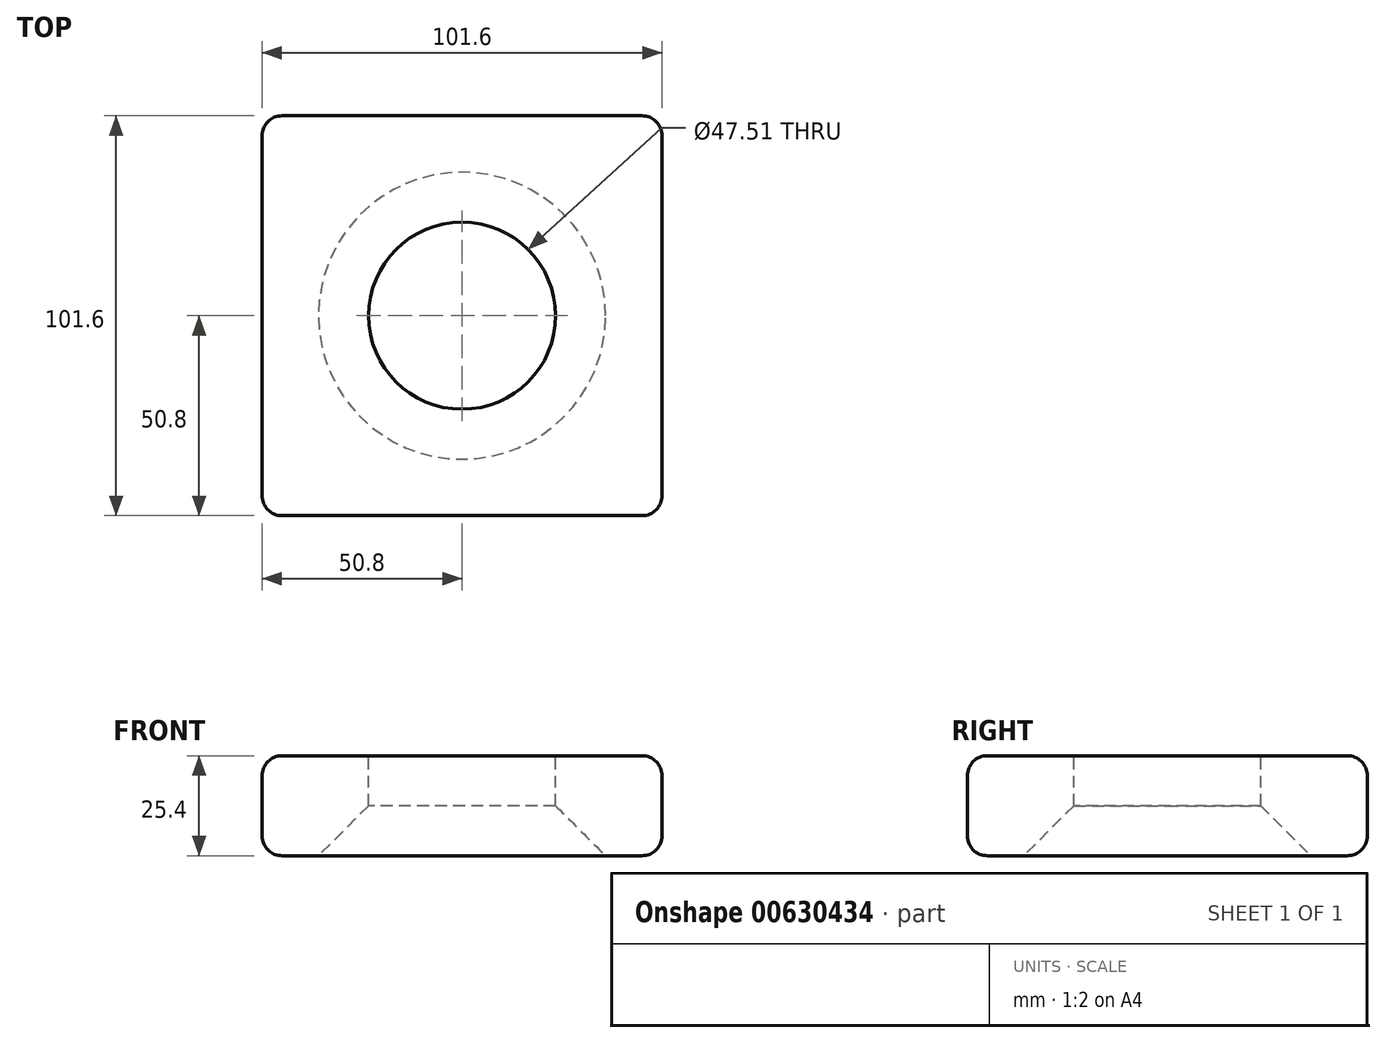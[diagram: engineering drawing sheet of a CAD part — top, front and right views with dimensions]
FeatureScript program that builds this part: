
annotation { "Feature Type Name" : "Feature", "Feature Type Description" : "" }
export const myFeature = defineFeature(function(context is Context, id is Id, definition is map)
    precondition{}
    {
        {
            var Q0;
            Q0=qCreatedBy(makeId("Top.planeOp"),FACE);
            var sketch = newSketch(context, id + "F0", { "sketchPlane" : qUnion([Q0])});
            skLineSegment(sketch, "E0.bottom", {"start": v(-50.8, 50.8) * mm, "end": v(50.8, 50.8) * mm});
            skLineSegment(sketch, "E0.top", {"start": v(-50.8, -50.8) * mm, "end": v(50.8, -50.8) * mm});
            skLineSegment(sketch, "E0.left", {"start": v(-50.8, 50.8) * mm, "end": v(-50.8, -50.8) * mm});
            skLineSegment(sketch, "E0.right", {"start": v(50.8, 50.8) * mm, "end": v(50.8, -50.8) * mm});
            skSolve(sketch);
        }
        {
            var Q0;
            Q0=makeQuery(id+"F0.imprint","IMPRINT",FACE,{"disambiguationData":[TD([[makeQuery(id+"F0.imprint","IMPRINT",EDGE,{"derivedFrom":sQuery(id+"F0.wireOp",EDGE,"E0.bottom")}),-1.0]])]});
            extrude(context, id + "F1", {"entities" : qUnion([Q0]), "oppositeDirection" : true, "depth" : 25.4 * mm, "offsetDistance" : 25.4 * mm});
        }
        {
            var Q0;
            Q0=makeQuery(id+"F1.opExtrude","CAP_FACE",FACE,{"disambiguationData":[OSD([sQuery(id+"F0.wireOp",EDGE,"E0.bottom"),sQuery(id+"F0.wireOp",EDGE,"E0.top"),sQuery(id+"F0.wireOp",EDGE,"E0.left"),sQuery(id+"F0.wireOp",EDGE,"E0.right")])],"isStart":true});
            var sketch = newSketch(context, id + "F2", { "sketchPlane" : qUnion([Q0])});
            skCircle(sketch, "E1", {"center": v(0, 0) * mm, "radius": 23.76 * mm});
            skSolve(sketch);
        }
        {
            var Q0;
            Q0=makeQuery(id+"F2.imprint","IMPRINT",FACE,{"disambiguationData":[TD([[makeQuery(id+"F2.imprint","IMPRINT",EDGE,{"derivedFrom":sQuery(id+"F2.wireOp",EDGE,"E1")}),1.0]])]});
            extrude(context, id + "F3", {"entities" : qUnion([Q0]), "operationType" : NewBodyOperationType.REMOVE, "endBound" : BoundingType.THROUGH_ALL, "oppositeDirection" : true, "depth" : 25.4 * mm, "offsetDistance" : 25.4 * mm});
        }
        {
            var Q0;
            Q0=makeQuery(id+"F1.opExtrude","SWEPT_EDGE",EDGE,{"disambiguationData":[OSD([sQuery(id+"F0.wireOp",EDGE,"E0.top"),sQuery(id+"F0.wireOp",EDGE,"E0.right")])]});
            var Q1;
            Q1=makeQuery(id+"F1.opExtrude","SWEPT_EDGE",EDGE,{"disambiguationData":[OSD([sQuery(id+"F0.wireOp",EDGE,"E0.top"),sQuery(id+"F0.wireOp",EDGE,"E0.left")])]});
            var Q2;
            Q2=makeQuery(id+"F1.opExtrude","SWEPT_EDGE",EDGE,{"disambiguationData":[OSD([sQuery(id+"F0.wireOp",EDGE,"E0.bottom"),sQuery(id+"F0.wireOp",EDGE,"E0.right")])]});
            var Q3;
            Q3=makeQuery(id+"F3.boolean.opBoolean","COPY",EDGE,{"derivedFrom":makeQuery(id+"F3.opExtrude","CAP_EDGE",EDGE,{"disambiguationData":[OSD([sQuery(id+"F2.wireOp",EDGE,"E1")])],"isStart":true})});
            var Q4;
            Q4=makeQuery(id+"F1.opExtrude","SWEPT_EDGE",EDGE,{"disambiguationData":[OSD([sQuery(id+"F0.wireOp",EDGE,"E0.bottom"),sQuery(id+"F0.wireOp",EDGE,"E0.left")])]});
            fillet(context, id + "F4", {"entities" : qUnion([Q0, Q1, Q2, Q3, Q4]), "radius" : 5.08 * mm, "tangentPropagation" : true, "allowEdgeOverflow" : false});
        }
        {
            var Q0;
            Q0=makeQuery(id+"F1.opExtrude","SWEPT_FACE",FACE,{"disambiguationData":[OSD([sQuery(id+"F0.wireOp",EDGE,"E0.left")])]});
            fillet(context, id + "F5", {"entities" : qUnion([Q0]), "radius" : 5.08 * mm, "tangentPropagation" : true, "allowEdgeOverflow" : false});
        }
        {
            var Q0;
            Q0=makeQuery(id+"F3.boolean.opBoolean","INTERSECT",EDGE,{"derivedFrom":[makeQuery(id+"F1.opExtrude","CAP_FACE",FACE,{"disambiguationData":[OSD([sQuery(id+"F0.wireOp",EDGE,"E0.bottom"),sQuery(id+"F0.wireOp",EDGE,"E0.top"),sQuery(id+"F0.wireOp",EDGE,"E0.left"),sQuery(id+"F0.wireOp",EDGE,"E0.right")])],"isStart":false}),makeQuery(id+"F3.opExtrude","SWEPT_FACE",FACE,{"disambiguationData":[OSD([sQuery(id+"F2.wireOp",EDGE,"E1")])]})]});
            var Q1;
            {var subQ0=sQuery(id+"F2.wireOp",EDGE,"E1");Q1=makeQuery(id+"F4.opFillet","BLEND_EDGE",EDGE,{"blendedFrom":[makeQuery(id+"F3.boolean.opBoolean","COPY",EDGE,{"derivedFrom":makeQuery(id+"F3.opExtrude","CAP_EDGE",EDGE,{"disambiguationData":[OSD([subQ0])],"isStart":true})}),makeQuery(id+"F3.boolean.opBoolean","COPY",FACE,{"derivedFrom":makeQuery(id+"F3.opExtrude","SWEPT_FACE",FACE,{"disambiguationData":[OSD([subQ0])]})})],"blendedInto":[makeQuery(id+"F3.boolean.opBoolean","COPY",FACE,{"derivedFrom":makeQuery(id+"F3.opExtrude","SWEPT_FACE",FACE,{"disambiguationData":[OSD([subQ0])]})})]});}
            chamfer(context, id + "F6", {"entities" : qUnion([Q0, Q1]), "width" : 12.7 * mm, "tangentPropagation" : true});
        }
    });
